# Revit family: Showerhead-American_Standard-Traditional-1660.113_Series
name_source: partatom
category: Plumbing Fixtures
revit_build: Autodesk Revit 2015 (Build: 20140606_1530(x64)
units: mm (PartAtom-declared; Revit-internal decimal feet)

## types (3) — shared parameters
Assembly Code = D2010700
CW Connection = Yes
CWFU = 2
Default Elevation = 0"
Description = Flowise Traditional 3 Function Water Saving SH
Flow Rate = 1.5 gpm (5.7 L/min)
HW Connection = Yes
HWFU = 3
Height = 4 3/4"
Length = 4 1/2"
Manufacturer = American Standard
NPT Connection Size = 1/2"
Price = Prices may vary. Please consult Manufacturer Representative for most up-to-date price list.
Product Documentation Link = https://www.americanstandard-us.com
Product Page URL = https://www.americanstandard-us.com
URL = https://www.americanstandard-us.com
Vent Connection = No
WFU = 4
Waste Connection = Yes

## per-type parameters (varying)
| type | Finish | Material |
| 1660.113.002 | Brass-American Standard-002-Polished Chrome | Brass-American Standard-002-Polished Chrome |
| 1660.113.295 | Brass-American Standard-295-Brushed Nickel | Brass-American Standard-295-Brushed Nickel |
| 1660.113.224 | Brass-American Standard-224-Oil-Rubbed Bronze | Brass-American Standard-224-Oil-Rubbed Bronze |

note: column(s) folded — value = type name in every type: Model

## geometry (parser evidence)
native form markers: Sweep x3
no freeform markers — native parametric forms only
